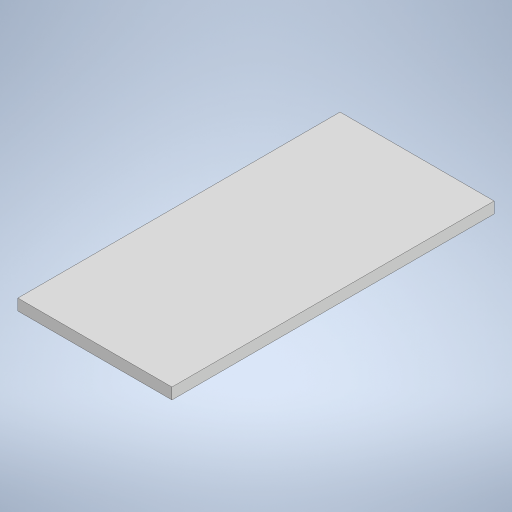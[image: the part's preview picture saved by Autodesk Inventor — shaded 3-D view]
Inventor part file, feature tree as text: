
AUTODESK INVENTOR PART (.ipt)
format: ipt  version: 2023 (Build 270158000, 158)  size: 202,752 bytes
history: native  units: mm
features: other x1, extrude x1, sketch x1
ambient origin geometry x8: Origin, YZ Plane, XZ Plane, XY Plane, X Axis, Y Axis, Z Axis, Center Point
bodies: Body1 (feature_tree)
feature tree (3):
  other  "Bryła1"
  extrude  "Wyciągnięcie proste1"  Depth=22.0mm
  sketch  "Szkic1"
